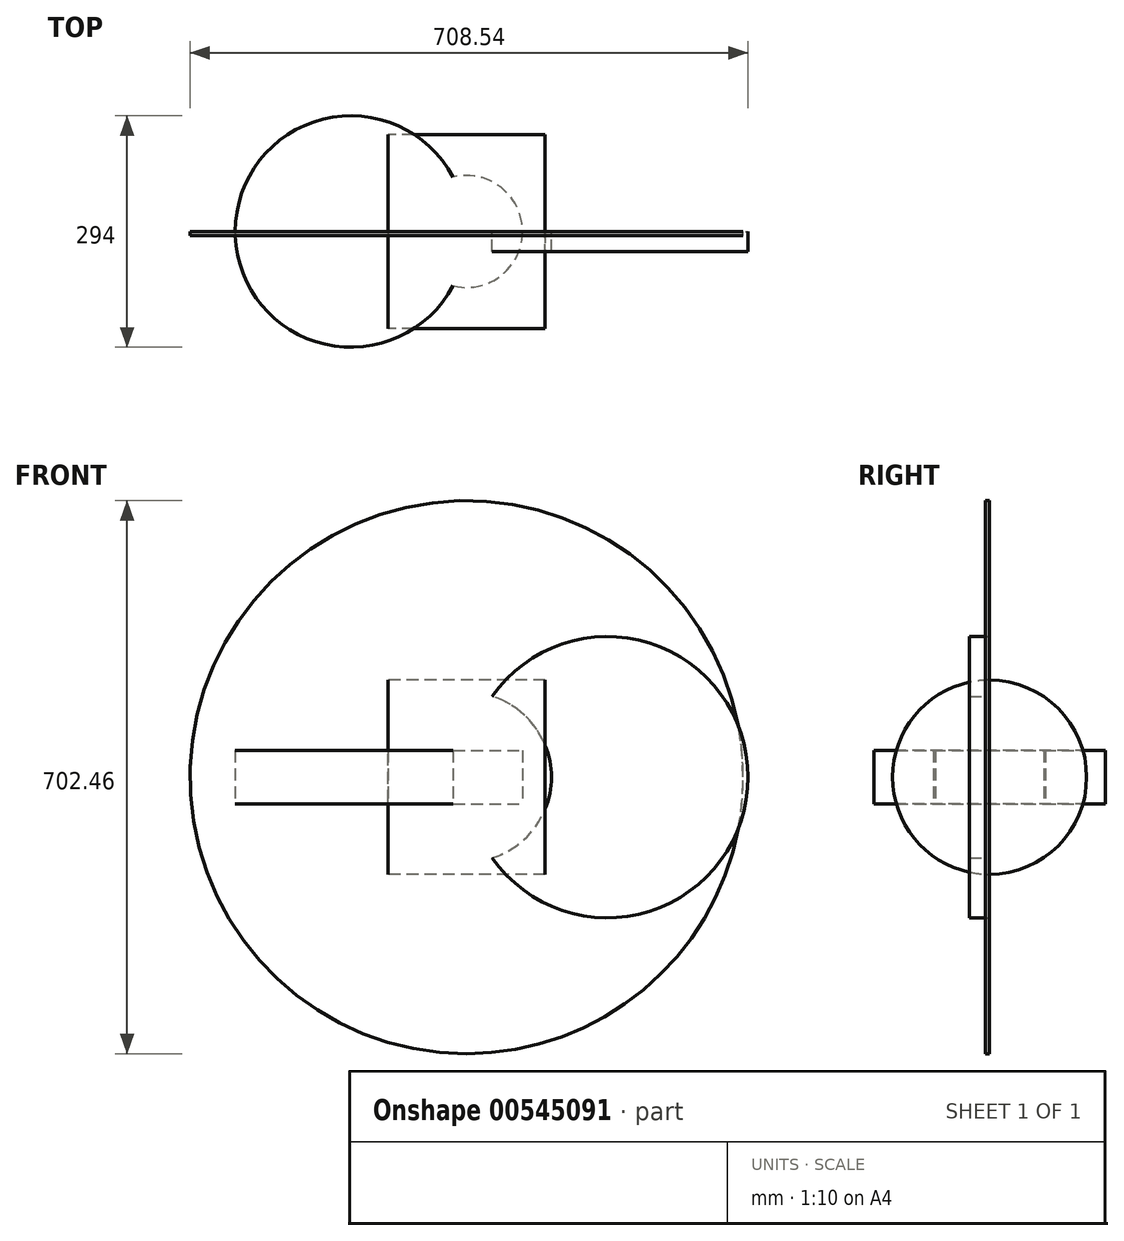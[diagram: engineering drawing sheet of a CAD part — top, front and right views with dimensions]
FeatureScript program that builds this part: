
annotation { "Feature Type Name" : "Feature", "Feature Type Description" : "" }
export const myFeature = defineFeature(function(context is Context, id is Id, definition is map)
    precondition{}
    {
        {
            var Q0;
            Q0=qCreatedBy(makeId("Front.planeOp"),FACE);
            var sketch = newSketch(context, id + "F0", { "sketchPlane" : qUnion([Q0])});
            skCircle(sketch, "E0", {"center": v(0, 0) * mm, "radius": 107.71 * mm});
            skCircle(sketch, "E1", {"center": v(178.66, 0) * mm, "radius": 178.66 * mm});
            skSolve(sketch);
        }
        {
            var Q0;
            Q0=qCreatedBy(makeId("Top.planeOp"),FACE);
            var sketch = newSketch(context, id + "F1", { "sketchPlane" : qUnion([Q0])});
            skCircle(sketch, "E2", {"center": v(-147, 0) * mm, "radius": 147 * mm});
            skCircle(sketch, "E3", {"center": v(0, 0) * mm, "radius": 71.14 * mm});
            skSolve(sketch);
        }
        {
            var Q0;
            Q0=qCreatedBy(makeId("Right.planeOp"),FACE);
            var sketch = newSketch(context, id + "F2", { "sketchPlane" : qUnion([Q0])});
            skCircle(sketch, "E4", {"center": v(0, 0) * mm, "radius": 123.3 * mm});
            skSolve(sketch);
        }
        {
            var Q0;
            {var subQ0=sQuery(id+"F0.wireOp",EDGE,"E1");var subQ1=sQuery(id+"F0.wireOp",EDGE,"E0");var subQ2=makeQuery(id+"F0.imprint","INTERSECT",VERTEX,{"disambiguationData":[OD(0.0)],"derivedFrom":[subQ1,subQ0]});Q0=makeQuery(id+"F0.imprint","IMPRINT",FACE,{"disambiguationData":[TD([[makeQuery(id+"F0.imprint","IMPRINT",EDGE,{"disambiguationData":[TD([[subQ2,-1.0]])],"derivedFrom":subQ1}),-1.0]])]});}
            extrude(context, id + "F3", {"entities" : qUnion([Q0]), "depth" : 25.4 * mm, "offsetDistance" : 25.4 * mm});
        }
        {
            var Q0;
            Q0 = qSketchRegion(id + "F1", true);
            extrude(context, id + "F4", {"entities" : qUnion([Q0]), "endBound" : BoundingType.SYMMETRIC, "depth" : 67.9 * mm, "offsetDistance" : 25.4 * mm});
        }
        {
            var Q0;
            Q0=makeQuery(id+"F2.imprint","IMPRINT",FACE,{"disambiguationData":[TD([[makeQuery(id+"F2.imprint","IMPRINT",EDGE,{"derivedFrom":sQuery(id+"F2.wireOp",EDGE,"E4")}),1.0]])]});
            extrude(context, id + "F5", {"entities" : qUnion([Q0]), "endBound" : BoundingType.SYMMETRIC, "depth" : 199.63 * mm, "offsetDistance" : 25.4 * mm});
        }
        {
            var Q0;
            Q0=qCreatedBy(makeId("Front.planeOp"),FACE);
            var sketch = newSketch(context, id + "F6", { "sketchPlane" : qUnion([Q0])});
            skCircle(sketch, "E5", {"center": v(0, 0) * mm, "radius": 351.23 * mm});
            skSolve(sketch);
        }
        {
            var Q0;
            Q0=makeQuery(id+"F6.imprint","IMPRINT",FACE,{"disambiguationData":[TD([[makeQuery(id+"F6.imprint","IMPRINT",EDGE,{"derivedFrom":sQuery(id+"F6.wireOp",EDGE,"E5")}),1.0]])]});
            extrude(context, id + "F7", {"entities" : qUnion([Q0]), "depth" : 5.5 * mm, "offsetDistance" : 25.4 * mm});
        }
    });
